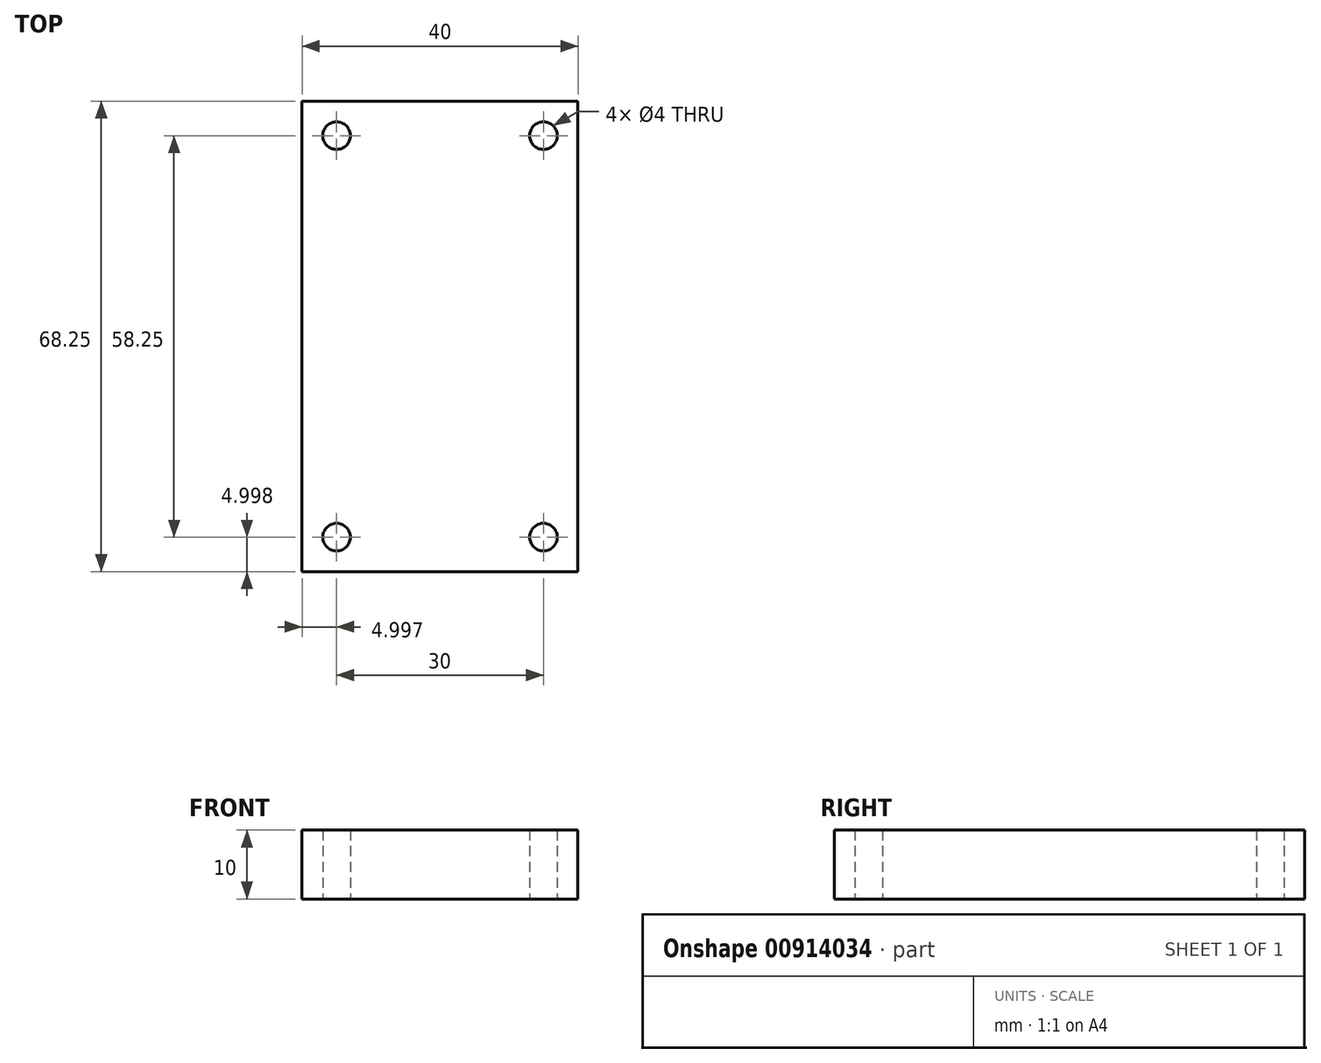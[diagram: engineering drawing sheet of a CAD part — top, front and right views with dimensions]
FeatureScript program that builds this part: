
annotation { "Feature Type Name" : "Feature", "Feature Type Description" : "" }
export const myFeature = defineFeature(function(context is Context, id is Id, definition is map)
    precondition{}
    {
        {
            var Q0;
            Q0=qCreatedBy(makeId("Top.planeOp"),FACE);
            var sketch = newSketch(context, id + "F0", { "sketchPlane" : qUnion([Q0])});
            skLineSegment(sketch, "E0.bottom", {"start": v(-27.63, 51.08) * mm, "end": v(12.37, 51.08) * mm});
            skLineSegment(sketch, "E0.top", {"start": v(-27.63, -17.17) * mm, "end": v(12.37, -17.17) * mm});
            skLineSegment(sketch, "E0.left", {"start": v(-27.63, 51.08) * mm, "end": v(-27.63, -17.17) * mm});
            skLineSegment(sketch, "E0.right", {"start": v(12.37, 51.08) * mm, "end": v(12.37, -17.17) * mm});
            skCircle(sketch, "E1", {"center": v(-22.63, 46.08) * mm, "radius": 2 * mm});
            skCircle(sketch, "E2", {"center": v(7.37, 46.08) * mm, "radius": 2 * mm});
            skCircle(sketch, "E3", {"center": v(7.37, -12.17) * mm, "radius": 2 * mm});
            skCircle(sketch, "E4", {"center": v(-22.63, -12.17) * mm, "radius": 2 * mm});
            skSolve(sketch);
        }
        {
            var Q0;
            Q0=makeQuery(id+"F0.imprint","IMPRINT",FACE,{"disambiguationData":[TD([[makeQuery(id+"F0.imprint","IMPRINT",EDGE,{"derivedFrom":sQuery(id+"F0.wireOp",EDGE,"E0.bottom")}),-1.0]])]});
            extrude(context, id + "F1", {"entities" : qUnion([Q0]), "depth" : 10 * mm, "offsetDistance" : 25 * mm});
        }
    });
